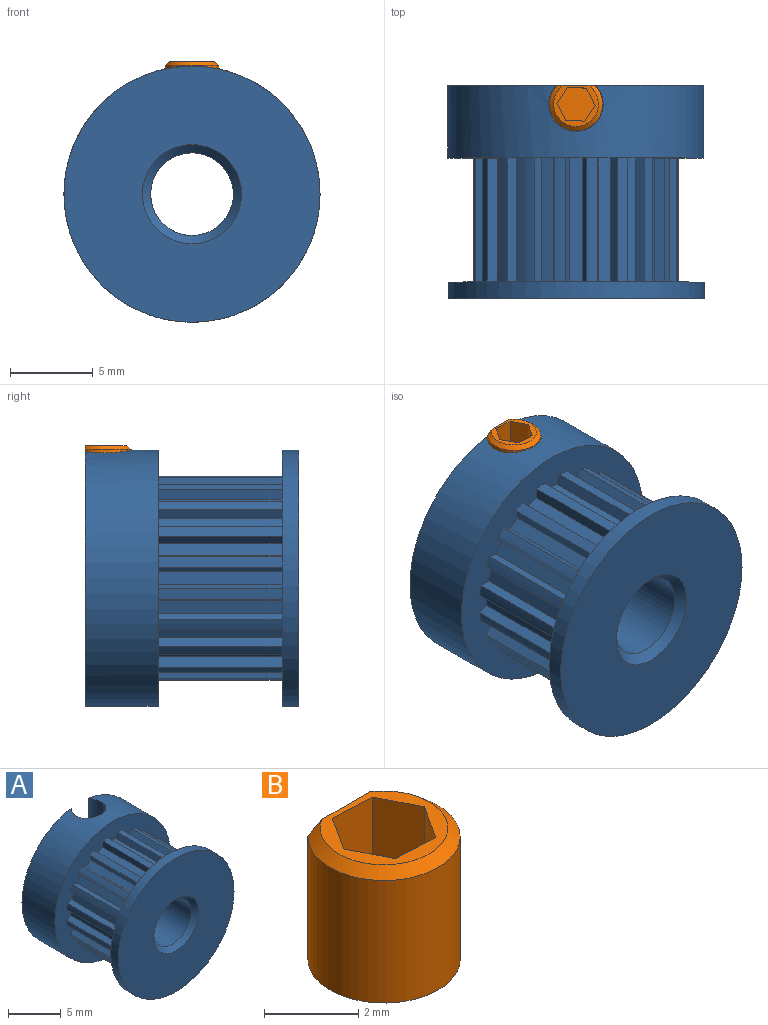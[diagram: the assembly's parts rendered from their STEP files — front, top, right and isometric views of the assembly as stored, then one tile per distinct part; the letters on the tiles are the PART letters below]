
ASSEMBLY  parts=2 mates=1
PART A: 89 faces, bbox 15.5x12.9x15.5 mm
  f0: plane 7.5x0.64mm, normal (1,0,-0.08), area 4.8mm2, adj f1,f2,f80,f87
  f1: plane 7.5x0.76mm, normal (0.31,0,-0.95), area 6mm2, adj f0,f3,f80,f87
  f2: cylinder r=6.21mm len=7.5mm, axis (0,1,0), area 4.9mm2, adj f0,f4,f80,f87
  f3: plane 7.5x0.49mm, normal (-0.76,0,-0.65), area 4.8mm2, adj f1,f5,f80,f87
  f4: plane 7.5x0.59mm, normal (-0.92,0,-0.38), area 4.8mm2, adj f2,f6,f80,f87
  f5: cylinder r=6.21mm len=7.5mm, axis (0,1,0), area 4.9mm2, adj f3,f7,f80,f87
  f6: plane 7.5x0.8mm, normal (0,0,-1), area 6mm2, adj f4,f8,f80,f87
  f7: plane 7.5x0.63mm, normal (0.97,0,0.23), area 4.8mm2, adj f5,f9,f80,f87
  f8: plane 7.5x0.59mm, normal (0.92,0,-0.38), area 4.8mm2, adj f6,f10,f80,f87
  f9: plane 7.5x0.65mm, normal (0.59,0,-0.81), area 6mm2, adj f7,f11,f80,f87
  f10: cylinder r=6.21mm len=7.5mm, axis (0,1,0), area 4.9mm2, adj f8,f12,f80,f87
  f11: plane 7.5x0.55mm, normal (-0.52,0,-0.85), area 4.8mm2, adj f9,f13,f80,f87
  f12: plane 7.5x0.64mm, normal (-1,0,-0.08), area 4.8mm2, adj f10,f14,f80,f87
  f13: cylinder r=6.21mm len=7.5mm, axis (0,1,0), area 4.9mm2, adj f11,f15,f80,f87
  f14: plane 7.5x0.76mm, normal (-0.31,0,-0.95), area 6mm2, adj f12,f16,f80,f87
  f15: plane 7.5x0.55mm, normal (0.85,0,0.52), area 4.8mm2, adj f13,f17,f80,f87
  f16: plane 7.5x0.49mm, normal (0.76,0,-0.65), area 4.8mm2, adj f14,f18,f80,f87
  f17: plane 7.5x0.65mm, normal (0.81,0,-0.59), area 6mm2, adj f15,f19,f80,f87
  f18: cylinder r=6.21mm len=7.5mm, axis (0,1,0), area 4.9mm2, adj f16,f20,f80,f87
  f19: plane 7.5x0.63mm, normal (-0.23,0,-0.97), area 4.8mm2, adj f17,f21,f80,f87
  f20: plane 7.5x0.63mm, normal (-0.97,0,0.23), area 4.8mm2, adj f18,f22,f80,f87
  f21: cylinder r=6.21mm len=7.5mm, axis (0,1,0), area 4.9mm2, adj f19,f23,f80,f87
  f22: plane 7.5x0.65mm, normal (-0.59,0,-0.81), area 6mm2, adj f20,f24,f80,f87
  f23: plane 7.5x0.49mm, normal (0.65,0,0.76), area 4.8mm2, adj f21,f25,f80,f87
  f24: plane 7.5x0.55mm, normal (0.52,0,-0.85), area 4.8mm2, adj f22,f26,f80,f87
  f25: plane 7.5x0.76mm, normal (0.95,0,-0.31), area 6mm2, adj f23,f27,f80,f87
  f26: cylinder r=6.21mm len=7.5mm, axis (0,1,0), area 4.9mm2, adj f24,f28,f80,f87
  f27: plane 7.5x0.64mm, normal (0.08,0,-1), area 4.8mm2, adj f25,f29,f80,f87
  f28: plane 7.5x0.55mm, normal (-0.85,0,0.52), area 4.8mm2, adj f26,f30,f80,f87
  f29: cylinder r=6.21mm len=7.5mm, axis (0,1,0), area 4.9mm2, adj f27,f31,f80,f87
  f30: plane 7.5x0.65mm, normal (-0.81,0,-0.59), area 6mm2, adj f28,f32,f80,f87
  f31: plane 7.5x0.59mm, normal (0.38,0,0.92), area 4.8mm2, adj f29,f33,f80,f87
  f32: plane 7.5x0.63mm, normal (0.23,0,-0.97), area 4.8mm2, adj f30,f34,f80,f87
  f33: plane 7.5x0.8mm, normal (1,0,0), area 6mm2, adj f31,f35,f80,f87
  f34: cylinder r=6.21mm len=7.5mm, axis (0,1,0), area 4.9mm2, adj f32,f36,f80,f87
  f35: plane 7.5x0.59mm, normal (0.38,0,-0.92), area 4.8mm2, adj f33,f37,f80,f87
  f36: plane 7.5x0.49mm, normal (-0.65,0,0.76), area 4.8mm2, adj f34,f38,f80,f87
  f37: cylinder r=6.21mm len=7.5mm, axis (0,1,0), area 4.9mm2, adj f35,f39,f80,f87
  f38: plane 7.5x0.76mm, normal (-0.95,0,-0.31), area 6mm2, adj f36,f40,f80,f87
  f39: plane 7.5x0.64mm, normal (0.08,0,1), area 4.8mm2, adj f37,f41,f80,f87
  f40: plane 7.5x0.64mm, normal (-0.08,0,-1), area 4.8mm2, adj f38,f42,f80,f87
  f41: plane 7.5x0.76mm, normal (0.95,0,0.31), area 6mm2, adj f39,f43,f80,f87
  f42: cylinder r=6.21mm len=7.5mm, axis (0,1,0), area 4.9mm2, adj f40,f44,f80,f87
  f43: plane 7.5x0.49mm, normal (0.65,0,-0.76), area 4.8mm2, adj f41,f45,f80,f87
  f44: plane 7.5x0.59mm, normal (-0.38,0,0.92), area 4.8mm2, adj f42,f46,f80,f87
  f45: cylinder r=6.21mm len=7.5mm, axis (0,1,0), area 4.9mm2, adj f43,f47,f80,f87
  f46: plane 7.5x0.8mm, normal (-1,0,0), area 6mm2, adj f44,f48,f80,f87
  f47: plane 7.5x0.63mm, normal (-0.23,0,0.97), area 4.8mm2, adj f45,f49,f80,f87
  f48: plane 7.5x0.59mm, normal (-0.38,0,-0.92), area 4.8mm2, adj f46,f50,f80,f87
  f49: plane 7.5x0.65mm, normal (0.81,0,0.59), area 6mm2, adj f47,f51,f80,f87
  f50: cylinder r=6.21mm len=7.5mm, axis (0,1,0), area 4.9mm2, adj f48,f52,f80,f87
  f51: plane 7.5x0.55mm, normal (0.85,0,-0.52), area 4.8mm2, adj f49,f53,f80,f87
  f52: plane 7.5x0.64mm, normal (-0.08,0,1), area 4.8mm2, adj f50,f54,f80,f87
  f53: cylinder r=6.21mm len=7.5mm, axis (0,1,0), area 4.9mm2, adj f51,f55,f80,f87
  f54: plane 7.5x0.76mm, normal (-0.95,0,0.31), area 6mm2, adj f52,f56,f80,f87
  f55: plane 7.5x0.55mm, normal (-0.52,0,0.85), area 4.8mm2, adj f53,f57,f80,f87
  f56: plane 7.5x0.49mm, normal (-0.65,0,-0.76), area 4.8mm2, adj f54,f58,f80,f87
  f57: plane 7.5x0.65mm, normal (0.59,0,0.81), area 6mm2, adj f55,f59,f80,f87
  f58: cylinder r=6.21mm len=7.5mm, axis (0,1,0), area 4.9mm2, adj f56,f60,f80,f87
  f59: plane 7.5x0.63mm, normal (0.97,0,-0.23), area 4.8mm2, adj f57,f61,f80,f87
  f60: plane 7.5x0.63mm, normal (0.23,0,0.97), area 4.8mm2, adj f58,f62,f80,f87
  f61: cylinder r=6.21mm len=7.5mm, axis (0,1,0), area 4.9mm2, adj f59,f63,f80,f87
  f62: plane 7.5x0.65mm, normal (-0.81,0,0.59), area 6mm2, adj f60,f64,f80,f87
  f63: plane 7.5x0.49mm, normal (-0.76,0,0.65), area 4.8mm2, adj f61,f65,f80,f87
  f64: plane 7.5x0.55mm, normal (-0.85,0,-0.52), area 4.8mm2, adj f62,f66,f80,f87
  f65: plane 7.5x0.76mm, normal (0.31,0,0.95), area 6mm2, adj f63,f67,f80,f87
  f66: cylinder r=6.21mm len=7.5mm, axis (0,1,0), area 4.9mm2, adj f64,f68,f80,f87
  f67: plane 7.5x0.64mm, normal (1,0,0.08), area 4.8mm2, adj f65,f69,f80,f87
  f68: plane 7.5x0.55mm, normal (0.52,0,0.85), area 4.8mm2, adj f66,f70,f80,f87
  f69: cylinder r=6.21mm len=7.5mm, axis (0,1,0), area 4.9mm2, adj f67,f71,f80,f87
  f70: plane 7.5x0.65mm, normal (-0.59,0,0.81), area 6mm2, adj f68,f72,f80,f87
  f71: plane 7.5x0.59mm, normal (-0.92,0,0.38), area 4.8mm2, adj f69,f73,f80,f87
  f72: plane 7.5x0.63mm, normal (-0.97,0,-0.23), area 4.8mm2, adj f70,f74,f80,f87
  f73: plane 7.5x0.8mm, normal (0,0,1), area 6mm2, adj f71,f77,f80,f87
  f74: cylinder r=6.21mm len=7.5mm, axis (0,1,0), area 4.9mm2, adj f72,f78,f80,f87
  f75: plane 15.5x15.5mm, normal (0,-1,0), area 160.4mm2, adj f76,f79
  f76: cylinder r=7.75mm len=15.5mm, axis (0,-1,0), area 48.7mm2, adj f75,f80
  f77: plane 7.5x0.59mm, normal (0.92,0,0.38), area 4.8mm2, adj f73,f80,f81,f87
  f78: plane 7.5x0.49mm, normal (0.76,0,0.65), area 4.8mm2, adj f74,f80,f82,f87
  f79: cone r=3mm half-angle=45deg, axis (0,-1,0), area 12.2mm2, adj f75,f83
  f80: plane 15.5x15.5mm, normal (0,1,0), area 80.4mm2, adj f0,f1,f2,f3,f4,f5,f6,f7
  f81: cylinder r=6.21mm len=7.5mm, axis (0,1,0), area 4.9mm2, adj f77,f80,f84,f87
  f82: plane 7.5x0.76mm, normal (-0.31,0,0.95), area 6mm2, adj f78,f80,f84,f87
  f83: cylinder r=2.5mm len=12.4mm, axis (0,-1,0), area 186.5mm2, adj f79,f85,f86
  f84: plane 7.5x0.64mm, normal (-1,0,0.08), area 4.8mm2, adj f80,f81,f82,f87
  f85: plane 15.5x15.41mm, normal (0,1,0), area 156.5mm2, adj f83,f86,f88
  f86: cylinder r=1.65mm len=5.87mm, axis (0,0,-1), area 42.6mm2, adj f83,f85,f88
  f87: plane 15.5x15.5mm, normal (0,-1,0), area 80.4mm2, adj f0,f1,f2,f3,f4,f5,f6,f7
  f88: cylinder r=7.75mm len=15.5mm, axis (0,1,0), area 206.5mm2, adj f85,f86,f87
PART B: 13 faces, bbox 3.3x3.3x4 mm
  f0: plane 3x1.15mm, normal (0.05,1,0), area 3.5mm2, adj f1,f2,f4,f8
  f1: plane 3x1.03mm, normal (0.89,0.46,0), area 3.5mm2, adj f0,f3,f4,f8
  f2: plane 3x0.97mm, normal (-0.84,0.54,0), area 3.5mm2, adj f0,f4,f5,f8
  f3: plane 3x0.97mm, normal (0.84,-0.54,0), area 3.5mm2, adj f1,f4,f6,f8
  f4: plane 2.31x2.06mm, normal (0,0,1), area 3.5mm2, adj f0,f1,f2,f3,f5,f6
  f5: plane 3x1.03mm, normal (-0.89,-0.46,0), area 3.5mm2, adj f2,f4,f6,f8
  f6: plane 3x1.15mm, normal (-0.05,-1,0), area 3.5mm2, adj f3,f4,f5,f8
  f7: plane 1.19x1.19mm, normal (0,0,-1), area 1.1mm2, adj f9
  f8: plane 2.71x2.5mm, normal (0,0,1), area 2.1mm2, adj f0,f1,f2,f3,f5,f6,f10,f11
  f9: cone r=1.61mm half-angle=59.8deg, axis (0,0,1), area 7.3mm2, adj f7,f10,f12
  f10: plane 3.72x2.3mm, normal (0,1,0), area 8mm2, adj f8,f9,f11,f12
  f11: cone r=1.61mm half-angle=48.9deg, axis (0,0,-1), area 2.5mm2, adj f8,f10,f12
  f12: cylinder r=1.61mm len=3.23mm, axis (0,0,-1), area 24.3mm2, adj f9,f10,f11
PLACE A at identity
PLACE B t=(0,0,-0.99)mm
MATE fastened B.f9 <-> A.f86  axis (0,0,-1) through (0,-3.25,7.79)mm
